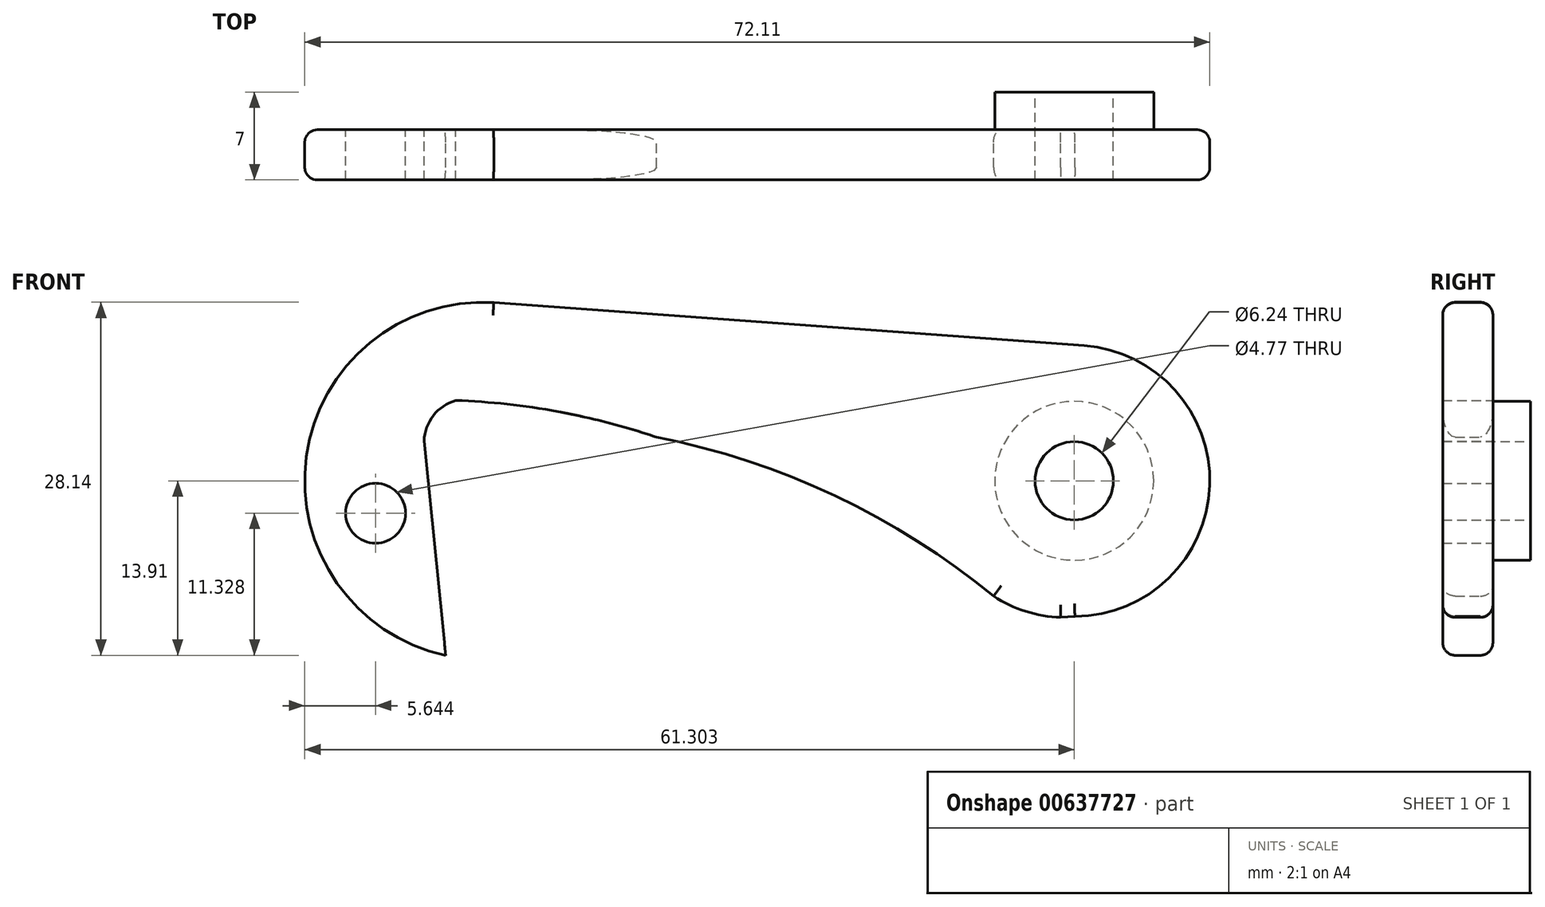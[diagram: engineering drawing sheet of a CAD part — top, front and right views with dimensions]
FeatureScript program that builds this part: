
annotation { "Feature Type Name" : "Feature", "Feature Type Description" : "" }
export const myFeature = defineFeature(function(context is Context, id is Id, definition is map)
    precondition{}
    {
        {
            var Q0;
            Q0=qCreatedBy(makeId("Front.planeOp"),FACE);
            var sketch = newSketch(context, id + "F0", { "sketchPlane" : qUnion([Q0])});
            skArc(sketch, "E0", {"start": v(-20.72, 3.48) * mm, "mid": v(-44.76, 9.9) * mm, "end": v(-37.53, -13.91) * mm});
            skCircle(sketch, "E1", {"center": v(12.54, 0) * mm, "radius": 10.8 * mm});
            skLineSegment(sketch, "E2", {"start": v(-33.7, 14.2) * mm, "end": v(13.33, 10.77) * mm});
            skArc(sketch, "E3", {"start": v(-36.74, 6.41) * mm, "mid": v(-37.93, 5.8) * mm, "end": v(-38.8, 4.77) * mm});
            skLineSegment(sketch, "E4", {"start": v(-39.26, 3.17) * mm, "end": v(-38.33, -6.03) * mm});
            skLineSegment(sketch, "E5", {"start": v(11.47, -10.89) * mm, "end": v(12.6, -10.8) * mm});
            skArc(sketch, "E6", {"start": v(-20.72, 3.48) * mm, "mid": v(-28.62, 5.52) * mm, "end": v(-36.74, 6.41) * mm});
            skLineSegment(sketch, "E7", {"start": v(-38.33, -6.03) * mm, "end": v(-37.53, -13.91) * mm});
            skArc(sketch, "E8", {"start": v(-38.8, 4.77) * mm, "mid": v(-39.13, 4) * mm, "end": v(-39.26, 3.17) * mm});
            skPoint(sketch, "E9.start.orphan", {"position": v(-34.53, -14.23) * mm});
            skArc(sketch, "E10", {"start": v(6.12, -9.18) * mm, "mid": v(-6.52, -1.2) * mm, "end": v(-20.72, 3.48) * mm});
            skArc(sketch, "E11", {"start": v(4.7, -8.05) * mm, "mid": v(7.82, -10.09) * mm, "end": v(11.47, -10.89) * mm});
            skCircle(sketch, "E12", {"center": v(12.54, 0) * mm, "radius": 3.12 * mm});
            skCircle(sketch, "E13", {"center": v(-43.12, -2.58) * mm, "radius": 2.39 * mm});
            skCircle(sketch, "E14", {"center": v(-35.73, 3.03) * mm, "radius": 2.88 * mm});
            skSolve(sketch);
        }
        {
            var Q0;
            Q0=makeQuery(id+"F0.imprint","IMPRINT",FACE,{"disambiguationData":[TD([[makeQuery(id+"F0.imprint","IMPRINT",EDGE,{"derivedFrom":sQuery(id+"F0.wireOp",EDGE,"E12")}),-1.0]])]});
            var Q1;
            {var subQ0=sQuery(id+"F0.wireOp",EDGE,"E5");Q1=makeQuery(id+"F0.imprint","IMPRINT",FACE,{"disambiguationData":[TD([[makeQuery(id+"F0.imprint","IMPRINT",EDGE,{"derivedFrom":subQ0}),1.0]])]});}
            var Q2;
            Q2=makeQuery(id+"F0.imprint","IMPRINT",FACE,{"disambiguationData":[TD([[makeQuery(id+"F0.imprint","IMPRINT",EDGE,{"derivedFrom":sQuery(id+"F0.wireOp",EDGE,"E3")}),-1.0]])]});
            extrude(context, id + "F1", {"entities" : qUnion([Q0, Q1, Q2]), "depth" : 4 * mm, "offsetDistance" : 25 * mm});
        }
        {
            var Q0;
            Q0=makeQuery(id+"F1.opExtrude","CAP_FACE",FACE,{"disambiguationData":[OSD([sQuery(id+"F0.wireOp",EDGE,"E0"),sQuery(id+"F0.wireOp",EDGE,"E1"),sQuery(id+"F0.wireOp",EDGE,"E2"),sQuery(id+"F0.wireOp",EDGE,"E3"),sQuery(id+"F0.wireOp",EDGE,"E4"),sQuery(id+"F0.wireOp",EDGE,"E5"),sQuery(id+"F0.wireOp",EDGE,"E6"),sQuery(id+"F0.wireOp",EDGE,"E7"),sQuery(id+"F0.wireOp",EDGE,"E8"),sQuery(id+"F0.wireOp",EDGE,"E10"),sQuery(id+"F0.wireOp",EDGE,"E11"),sQuery(id+"F0.wireOp",EDGE,"E12")])],"isStart":true});
            var sketch = newSketch(context, id + "F2", { "sketchPlane" : qUnion([Q0])});
            skCircle(sketch, "E15", {"center": v(-12.54, 0) * mm, "radius": 6.33 * mm});
            skSolve(sketch);
        }
        {
            var Q0;
            Q0=makeQuery(id+"F2.imprint","IMPRINT",FACE,{"disambiguationData":[TD([[makeQuery(id+"F2.imprint","IMPRINT",EDGE,{"derivedFrom":sQuery(id+"F2.wireOp",EDGE,"E15")}),1.0]])]});
            extrude(context, id + "F3", {"entities" : qUnion([Q0]), "operationType" : NewBodyOperationType.ADD, "depth" : 3 * mm, "offsetDistance" : 25 * mm});
        }
        {
            var Q0;
            Q0=makeQuery(id+"F1.opExtrude","CAP_EDGE",EDGE,{"disambiguationData":[OSD([sQuery(id+"F0.wireOp",EDGE,"E10")])],"isStart":false});
            var Q1;
            Q1=makeQuery(id+"F1.opExtrude","CAP_EDGE",EDGE,{"disambiguationData":[OSD([sQuery(id+"F0.wireOp",EDGE,"E11")])],"isStart":false});
            var Q2;
            Q2=makeQuery(id+"F1.opExtrude","CAP_EDGE",EDGE,{"disambiguationData":[OSD([sQuery(id+"F0.wireOp",EDGE,"E1")])],"isStart":false});
            var Q3;
            Q3=makeQuery(id+"F1.opExtrude","CAP_EDGE",EDGE,{"disambiguationData":[OSD([sQuery(id+"F0.wireOp",EDGE,"E0")])],"isStart":false});
            var Q4;
            Q4=makeQuery(id+"F1.opExtrude","CAP_EDGE",EDGE,{"disambiguationData":[OSD([sQuery(id+"F0.wireOp",EDGE,"E0")])],"isStart":true});
            var Q5;
            Q5=makeQuery(id+"F1.opExtrude","CAP_EDGE",EDGE,{"disambiguationData":[OSD([sQuery(id+"F0.wireOp",EDGE,"E2")])],"isStart":true});
            var Q6;
            Q6=makeQuery(id+"F1.opExtrude","CAP_EDGE",EDGE,{"disambiguationData":[OSD([sQuery(id+"F0.wireOp",EDGE,"E10")])],"isStart":true});
            var Q7;
            Q7=makeQuery(id+"F1.opExtrude","CAP_EDGE",EDGE,{"disambiguationData":[OSD([sQuery(id+"F0.wireOp",EDGE,"E11")])],"isStart":true});
            fillet(context, id + "F4", {"entities" : qUnion([Q0, Q1, Q2, Q3, Q4, Q5, Q6, Q7]), "tangentPropagation" : true, "radius" : 1 * mm, "defaultsChanged" : false, "vertexSettings" : [], "allowEdgeOverflow" : false});
        }
    });
